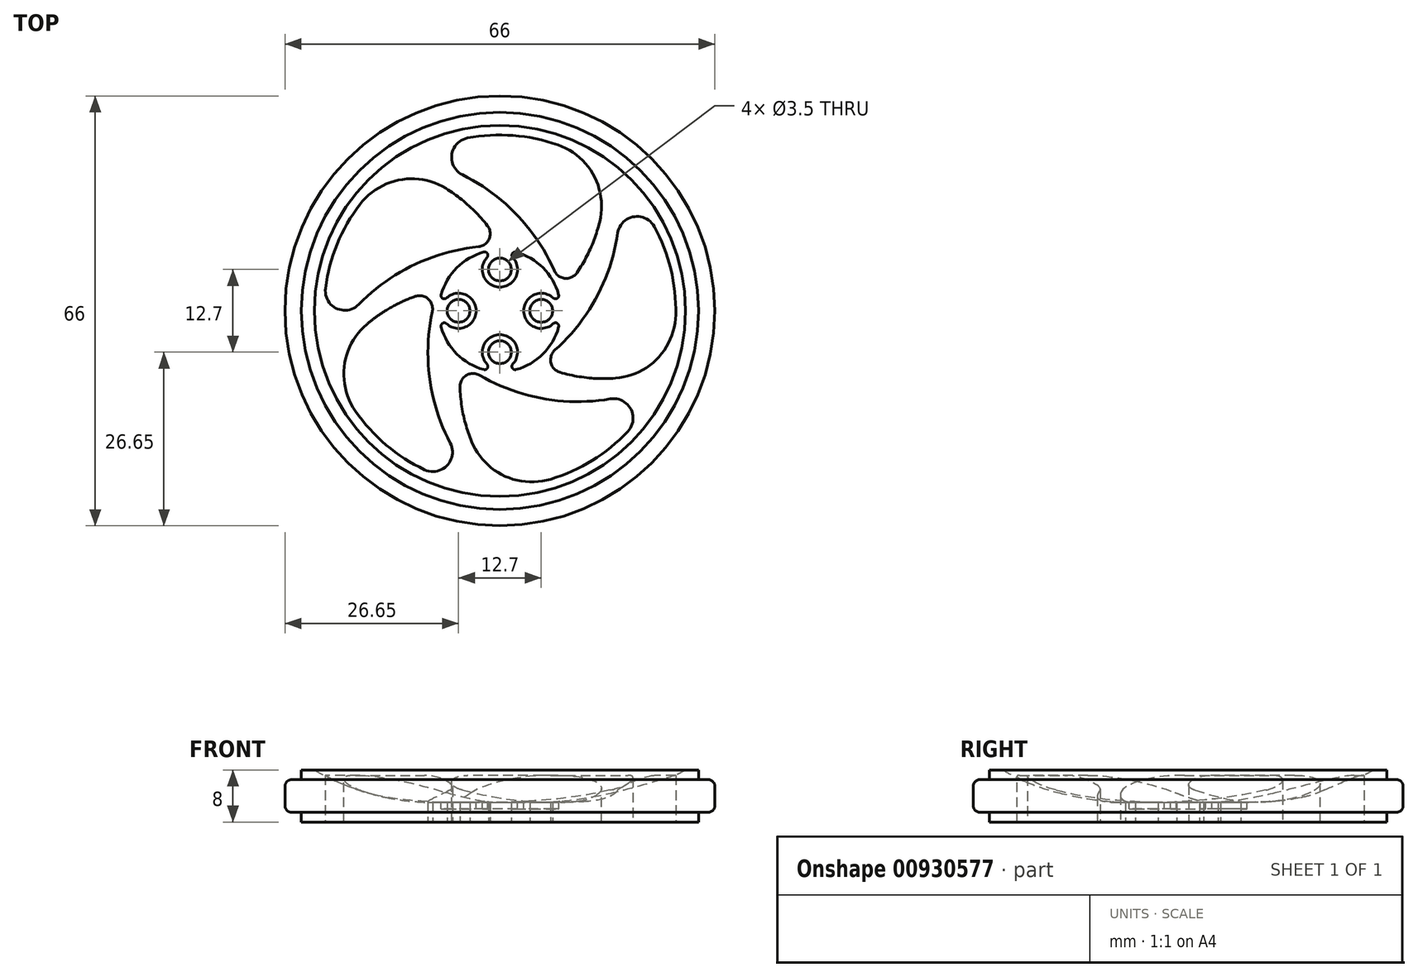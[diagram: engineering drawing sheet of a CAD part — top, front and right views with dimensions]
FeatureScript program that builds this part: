
annotation { "Feature Type Name" : "Feature", "Feature Type Description" : "" }
export const myFeature = defineFeature(function(context is Context, id is Id, definition is map)
    precondition{}
    {
        {
            var Q0;
            Q0=qCreatedBy(makeId("Front.planeOp"),FACE);
            var sketch = newSketch(context, id + "F0", { "sketchPlane" : qUnion([Q0])});
            skLineSegment(sketch, "E0.right", {"start": v(33, 1.5) * mm, "end": v(33, 6.5) * mm});
            skLineSegment(sketch, "E1", {"start": v(30.5, 6.5) * mm, "end": v(33, 6.5) * mm});
            skLineSegment(sketch, "E2", {"start": v(30.5, 6.5) * mm, "end": v(30.5, 8) * mm});
            skLineSegment(sketch, "E3.MirrorCS", {"start": v(30.5, 1.5) * mm, "end": v(30.5, 0) * mm});
            skLineSegment(sketch, "E4.MirrorCS", {"start": v(30.5, 1.5) * mm, "end": v(33, 1.5) * mm});
            skLineSegment(sketch, "E5.trimOffspring", {"start": v(28.5, 8) * mm, "end": v(30.5, 8) * mm});
            skLineSegment(sketch, "E6", {"start": v(0, 0) * mm, "end": v(30.5, 0) * mm});
            skLineSegment(sketch, "E7", {"start": v(0, 0) * mm, "end": v(0, 3) * mm});
            skLineSegment(sketch, "E8", {"start": v(0, 3) * mm, "end": v(10, 3) * mm});
            skArc(sketch, "E9", {"start": v(10, 3) * mm, "mid": v(19.58, 4.27) * mm, "end": v(28.5, 8) * mm});
            skSolve(sketch);
        }
        {
            var Q0;
            Q0=qSketchRegion(id+"F0",true);
            var Q1;
            Q1=sQuery(id+"F0.wireOp",EDGE,"E7");
            revolve(context, id + "F1", {"entities" : qUnion([Q0]), "axis" : qUnion([Q1]), "revolveType" : RevolveType.FULL});
        }
        {
            var Q0;
            Q0=makeQuery(id+"F1.opRevolve","SWEPT_EDGE",EDGE,{"disambiguationData":[OSD([sQuery(id+"F0.wireOp",EDGE,"E0.right"),sQuery(id+"F0.wireOp",EDGE,"E1")])]});
            var Q1;
            Q1=makeQuery(id+"F1.opRevolve","SWEPT_EDGE",EDGE,{"disambiguationData":[OSD([sQuery(id+"F0.wireOp",EDGE,"E0.right"),sQuery(id+"F0.wireOp",EDGE,"E4.MirrorCS")])]});
            fillet(context, id + "F2", {"entities" : qUnion([Q0, Q1]), "radius" : 1 * mm, "tangentPropagation" : true, "allowEdgeOverflow" : false});
        }
        {
            var Q0;
            Q0=makeQuery(id+"F1.opRevolve","SWEPT_FACE",FACE,{"disambiguationData":[OSD([sQuery(id+"F0.wireOp",EDGE,"E6")])]});
            var sketch = newSketch(context, id + "F3", { "sketchPlane" : qUnion([Q0])});
            skCircle(sketch, "E10", {"center": v(0, 0) * mm, "radius": 10 * mm, "construction": true});
            skCircle(sketch, "E11", {"center": v(0, 0) * mm, "radius": 28.5 * mm, "construction": true});
            skArc(sketch, "E12", {"start": v(-3, 26.83) * mm, "mid": v(-17.06, 20.93) * mm, "end": v(-25.68, 8.34) * mm});
            skArc(sketch, "E13.trimOffspring", {"start": v(-26.45, 5.44) * mm, "mid": v(-25.18, -9.76) * mm, "end": v(-15.87, -21.84) * mm});
            skArc(sketch, "E14.trimOffspring", {"start": v(18.2, -19.95) * mm, "mid": v(26.1, -6.9) * mm, "end": v(25.68, 8.34) * mm});
            skLineSegment(sketch, "E15", {"start": v(0, 28.5) * mm, "end": v(0, 0) * mm, "construction": true});
            skLineSegment(sketch, "E16", {"start": v(0, 0) * mm, "end": v(-25.68, 8.34) * mm, "construction": true});
            skLineSegment(sketch, "E17", {"start": v(0, 0) * mm, "end": v(25.68, 8.34) * mm, "construction": true});
            skLineSegment(sketch, "E18", {"start": v(0, 0) * mm, "end": v(-15.87, -21.84) * mm, "construction": true});
            skLineSegment(sketch, "E19", {"start": v(0, 0) * mm, "end": v(15.87, -21.84) * mm, "construction": true});
            skArc(sketch, "E20.trimOffspring", {"start": v(24.6, 11.14) * mm, "mid": v(14.63, 22.7) * mm, "end": v(0, 27) * mm});
            skArc(sketch, "E21.trimOffspring", {"start": v(-13.35, -23.47) * mm, "mid": v(1.5, -26.96) * mm, "end": v(15.87, -21.84) * mm});
            skArc(sketch, "E22", {"start": v(-3, 26.83) * mm, "mid": v(-10.37, 12.71) * mm, "end": v(-9.48, -3.2) * mm});
            skArc(sketch, "E23", {"start": v(-26.45, 5.44) * mm, "mid": v(-15.3, -5.93) * mm, "end": v(0.1, -10) * mm});
            skArc(sketch, "E24", {"start": v(-13.35, -23.47) * mm, "mid": v(0.92, -16.38) * mm, "end": v(9.54, -2.99) * mm});
            skArc(sketch, "E25", {"start": v(18.2, -19.95) * mm, "mid": v(15.86, -4.19) * mm, "end": v(5.8, 8.15) * mm});
            skArc(sketch, "E26", {"start": v(24.6, 11.14) * mm, "mid": v(8.89, 13.8) * mm, "end": v(-5.96, 8.03) * mm});
            skArc(sketch, "E27", {"start": v(0, 27) * mm, "mid": v(-5.04, 18.16) * mm, "end": v(-5.96, 8.03) * mm});
            skArc(sketch, "E28", {"start": v(-25.68, 8.34) * mm, "mid": v(-18.83, 0.82) * mm, "end": v(-9.48, -3.2) * mm});
            skArc(sketch, "E29", {"start": v(-15.87, -21.84) * mm, "mid": v(-6.6, -17.65) * mm, "end": v(0.1, -10) * mm});
            skArc(sketch, "E30", {"start": v(15.87, -21.84) * mm, "mid": v(14.75, -11.73) * mm, "end": v(9.54, -2.99) * mm});
            skArc(sketch, "E31", {"start": v(25.68, 8.34) * mm, "mid": v(15.71, 10.4) * mm, "end": v(5.8, 8.15) * mm});
            skCircle(sketch, "E32", {"center": v(0, -6.35) * mm, "radius": 1.75 * mm});
            skCircle(sketch, "E33", {"center": v(-6.35, 0) * mm, "radius": 1.75 * mm});
            skCircle(sketch, "E34", {"center": v(0, 6.35) * mm, "radius": 1.75 * mm});
            skCircle(sketch, "E35", {"center": v(6.35, 0) * mm, "radius": 1.75 * mm});
            skSolve(sketch);
        }
        {
            var Q0;
            Q0=qSketchRegion(id+"F3",true);
            extrude(context, id + "F4", {"entities" : qUnion([Q0]), "operationType" : NewBodyOperationType.REMOVE, "oppositeDirection" : true, "depth" : 25 * mm});
        }
        {
            var Q0;
            Q0=makeQuery(id+"F4.boolean.opBoolean","COPY",EDGE,{"derivedFrom":makeQuery(id+"F4.opExtrude","SWEPT_EDGE",EDGE,{"disambiguationData":[OSD([sQuery(id+"F3.wireOp",EDGE,"E12"),sQuery(id+"F3.wireOp",EDGE,"E22")])]})});
            var Q1;
            Q1=makeQuery(id+"F4.boolean.opBoolean","COPY",EDGE,{"derivedFrom":makeQuery(id+"F4.opExtrude","SWEPT_EDGE",EDGE,{"disambiguationData":[OSD([sQuery(id+"F3.wireOp",EDGE,"E20.trimOffspring"),sQuery(id+"F3.wireOp",EDGE,"E26")])]})});
            var Q2;
            Q2=makeQuery(id+"F4.boolean.opBoolean","COPY",EDGE,{"derivedFrom":makeQuery(id+"F4.opExtrude","SWEPT_EDGE",EDGE,{"disambiguationData":[OSD([sQuery(id+"F3.wireOp",EDGE,"E14.trimOffspring"),sQuery(id+"F3.wireOp",EDGE,"E25")])]})});
            var Q3;
            Q3=makeQuery(id+"F4.boolean.opBoolean","COPY",EDGE,{"derivedFrom":makeQuery(id+"F4.opExtrude","SWEPT_EDGE",EDGE,{"disambiguationData":[OSD([sQuery(id+"F3.wireOp",EDGE,"E21.trimOffspring"),sQuery(id+"F3.wireOp",EDGE,"E24")])]})});
            var Q4;
            Q4=makeQuery(id+"F4.boolean.opBoolean","COPY",EDGE,{"derivedFrom":makeQuery(id+"F4.opExtrude","SWEPT_EDGE",EDGE,{"disambiguationData":[OSD([sQuery(id+"F3.wireOp",EDGE,"E13.trimOffspring"),sQuery(id+"F3.wireOp",EDGE,"E23")])]})});
            fillet(context, id + "F5", {"entities" : qUnion([Q0, Q1, Q2, Q3, Q4]), "radius" : 3 * mm, "tangentPropagation" : true, "allowEdgeOverflow" : false});
        }
        {
            var Q0;
            Q0=makeQuery(id+"F4.boolean.opBoolean","COPY",EDGE,{"derivedFrom":makeQuery(id+"F4.opExtrude","SWEPT_EDGE",EDGE,{"disambiguationData":[OSD([sQuery(id+"F3.wireOp",EDGE,"E14.trimOffspring"),sQuery(id+"F3.wireOp",EDGE,"lH133nUo-b4dK-7Uis-ALbx-UH7YrD5dzAr5")])]})});
            var Q1;
            Q1=makeQuery(id+"F4.boolean.opBoolean","COPY",EDGE,{"derivedFrom":makeQuery(id+"F4.opExtrude","SWEPT_EDGE",EDGE,{"disambiguationData":[OSD([sQuery(id+"F3.wireOp",EDGE,"E20.trimOffspring"),sQuery(id+"F3.wireOp",EDGE,"Y5TeA7qx-hglw-YKO1-yJVa-Mu3tWydujS0s")])]})});
            var Q2;
            Q2=makeQuery(id+"F4.boolean.opBoolean","COPY",EDGE,{"derivedFrom":makeQuery(id+"F4.opExtrude","SWEPT_EDGE",EDGE,{"disambiguationData":[OSD([sQuery(id+"F3.wireOp",EDGE,"E12"),sQuery(id+"F3.wireOp",EDGE,"K8Gechwi-EIRI-6laA-ybGk-XkUKvmpAPVkA")])]})});
            var Q3;
            Q3=makeQuery(id+"F4.boolean.opBoolean","COPY",EDGE,{"derivedFrom":makeQuery(id+"F4.opExtrude","SWEPT_EDGE",EDGE,{"disambiguationData":[OSD([sQuery(id+"F3.wireOp",EDGE,"E13.trimOffspring"),sQuery(id+"F3.wireOp",EDGE,"yrZSpx71-NN5u-So2I-DmkD-7K2vPXZf8bNT")])]})});
            var Q4;
            Q4=makeQuery(id+"F4.boolean.opBoolean","COPY",EDGE,{"derivedFrom":makeQuery(id+"F4.opExtrude","SWEPT_EDGE",EDGE,{"disambiguationData":[OSD([sQuery(id+"F3.wireOp",EDGE,"E21.trimOffspring"),sQuery(id+"F3.wireOp",EDGE,"3wq5JMd6-PSVr-Z4Na-BiTl-nTZF3QSmccvR")])]})});
            fillet(context, id + "F6", {"entities" : qUnion([Q0, Q1, Q2, Q3, Q4]), "radius" : 10 * mm, "tangentPropagation" : true, "allowEdgeOverflow" : false});
        }
        {
            var Q0;
            Q0=makeQuery(id+"F4.boolean.opBoolean","COPY",EDGE,{"derivedFrom":makeQuery(id+"F4.opExtrude","SWEPT_EDGE",EDGE,{"disambiguationData":[OSD([sQuery(id+"F3.wireOp",EDGE,"E23"),sQuery(id+"F3.wireOp",EDGE,"E29")])]})});
            var Q1;
            Q1=makeQuery(id+"F4.boolean.opBoolean","COPY",EDGE,{"derivedFrom":makeQuery(id+"F4.opExtrude","SWEPT_EDGE",EDGE,{"disambiguationData":[OSD([sQuery(id+"F3.wireOp",EDGE,"E24"),sQuery(id+"F3.wireOp",EDGE,"E30")])]})});
            var Q2;
            Q2=makeQuery(id+"F4.boolean.opBoolean","COPY",EDGE,{"derivedFrom":makeQuery(id+"F4.opExtrude","SWEPT_EDGE",EDGE,{"disambiguationData":[OSD([sQuery(id+"F3.wireOp",EDGE,"E25"),sQuery(id+"F3.wireOp",EDGE,"E31")])]})});
            var Q3;
            Q3=makeQuery(id+"F4.boolean.opBoolean","COPY",EDGE,{"derivedFrom":makeQuery(id+"F4.opExtrude","SWEPT_EDGE",EDGE,{"disambiguationData":[OSD([sQuery(id+"F3.wireOp",EDGE,"E26"),sQuery(id+"F3.wireOp",EDGE,"E27")])]})});
            var Q4;
            Q4=makeQuery(id+"F4.boolean.opBoolean","COPY",EDGE,{"derivedFrom":makeQuery(id+"F4.opExtrude","SWEPT_EDGE",EDGE,{"disambiguationData":[OSD([sQuery(id+"F3.wireOp",EDGE,"E22"),sQuery(id+"F3.wireOp",EDGE,"E28")])]})});
            fillet(context, id + "F7", {"entities" : qUnion([Q0, Q1, Q2, Q3, Q4]), "radius" : 2 * mm, "tangentPropagation" : true, "allowEdgeOverflow" : false});
        }
        {
            var Q0;
            Q0=makeQuery(id+"F1.opRevolve","SWEPT_FACE",FACE,{"disambiguationData":[OSD([sQuery(id+"F0.wireOp",EDGE,"E8")])]});
            var sketch = newSketch(context, id + "F8", { "sketchPlane" : qUnion([Q0])});
            skArc(sketch, "E36", {"start": v(-9.02, -2.47) * mm, "mid": v(-6.61, -6.61) * mm, "end": v(-2.47, -9.02) * mm});
            skArc(sketch, "E37", {"start": v(-8.2, -1.97) * mm, "mid": v(-3.65, 0) * mm, "end": v(-8.2, 1.97) * mm});
            skArc(sketch, "E38", {"start": v(-1.97, 8.2) * mm, "mid": v(0, 3.65) * mm, "end": v(1.97, 8.2) * mm});
            skArc(sketch, "E39", {"start": v(8.2, 1.97) * mm, "mid": v(3.65, 0) * mm, "end": v(8.2, -1.97) * mm});
            skArc(sketch, "E40", {"start": v(1.97, -8.2) * mm, "mid": v(0, -3.65) * mm, "end": v(-1.97, -8.2) * mm});
            skArc(sketch, "E41", {"start": v(-9.02, 2.47) * mm, "mid": v(-8.8, 1.9) * mm, "end": v(-8.2, 1.97) * mm});
            skArc(sketch, "E42", {"start": v(-8.2, -1.97) * mm, "mid": v(-8.8, -1.9) * mm, "end": v(-9.02, -2.47) * mm});
            skArc(sketch, "E43", {"start": v(-1.97, 8.2) * mm, "mid": v(-1.9, 8.8) * mm, "end": v(-2.47, 9.02) * mm});
            skArc(sketch, "E44", {"start": v(2.47, 9.02) * mm, "mid": v(1.9, 8.8) * mm, "end": v(1.97, 8.2) * mm});
            skArc(sketch, "E45", {"start": v(8.2, 1.97) * mm, "mid": v(8.8, 1.9) * mm, "end": v(9.02, 2.47) * mm});
            skArc(sketch, "E46", {"start": v(9.02, -2.47) * mm, "mid": v(8.8, -1.9) * mm, "end": v(8.2, -1.97) * mm});
            skArc(sketch, "E47", {"start": v(-2.47, -9.02) * mm, "mid": v(-1.9, -8.8) * mm, "end": v(-1.97, -8.2) * mm});
            skArc(sketch, "E48", {"start": v(1.97, -8.2) * mm, "mid": v(1.9, -8.8) * mm, "end": v(2.47, -9.02) * mm});
            skArc(sketch, "E49.trimOffspring", {"start": v(-2.47, 9.02) * mm, "mid": v(-6.61, 6.61) * mm, "end": v(-9.02, 2.47) * mm});
            skArc(sketch, "E50.trimOffspring", {"start": v(9.02, 2.47) * mm, "mid": v(6.61, 6.61) * mm, "end": v(2.47, 9.02) * mm});
            skArc(sketch, "E51.trimOffspring", {"start": v(2.47, -9.02) * mm, "mid": v(6.61, -6.61) * mm, "end": v(9.02, -2.47) * mm});
            skSolve(sketch);
        }
        {
            var Q0;
            Q0=qSketchRegion(id+"F8",true);
            extrude(context, id + "F9", {"entities" : qUnion([Q0]), "operationType" : NewBodyOperationType.REMOVE, "oppositeDirection" : true, "depth" : 1 * mm});
        }
    });
